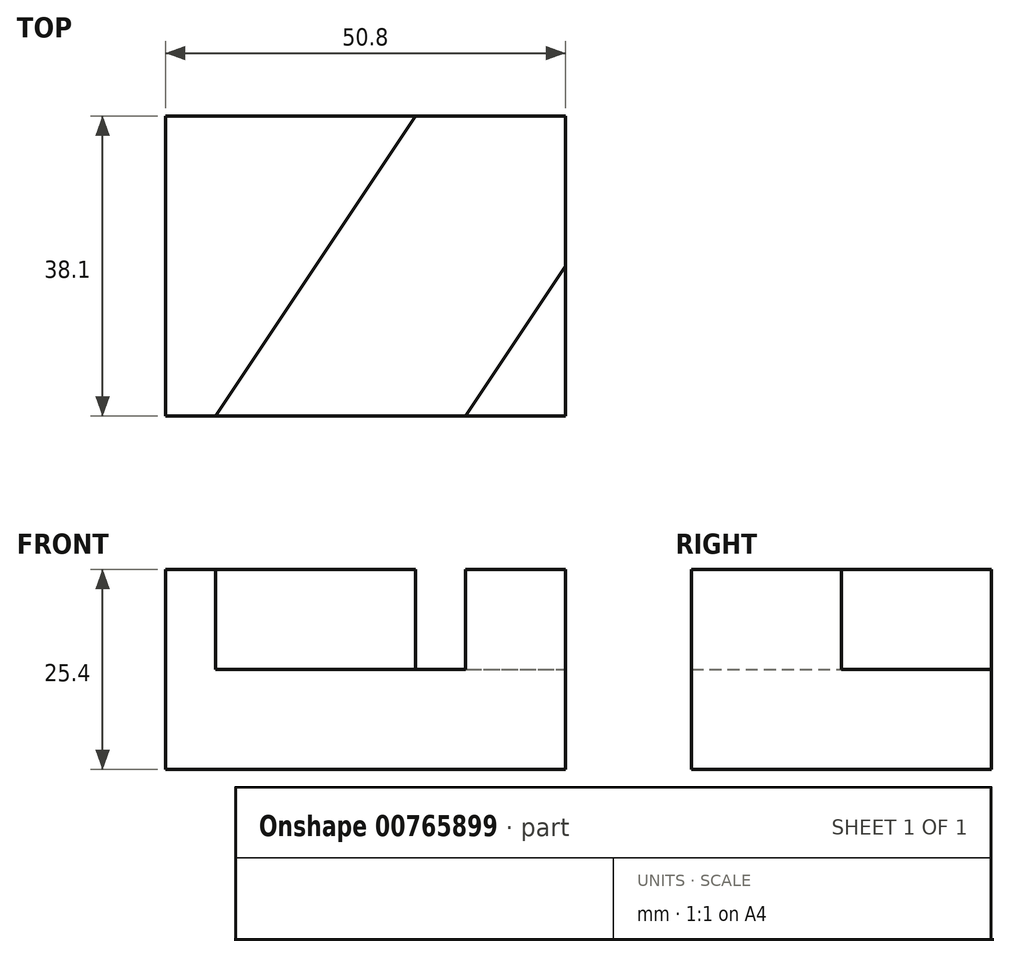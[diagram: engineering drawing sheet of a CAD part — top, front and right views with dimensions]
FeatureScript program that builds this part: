
annotation { "Feature Type Name" : "Feature", "Feature Type Description" : "" }
export const myFeature = defineFeature(function(context is Context, id is Id, definition is map)
    precondition{}
    {
        {
            var Q0;
            Q0=qCreatedBy(makeId("Top.planeOp"),FACE);
            var sketch = newSketch(context, id + "F0", { "sketchPlane" : qUnion([Q0])});
            skLineSegment(sketch, "E0", {"start": v(0, 0) * mm, "end": v(0, 38.1) * mm});
            skLineSegment(sketch, "E1", {"start": v(0, 38.1) * mm, "end": v(50.8, 38.1) * mm});
            skLineSegment(sketch, "E2", {"start": v(50.8, 38.1) * mm, "end": v(50.8, 0) * mm});
            skLineSegment(sketch, "E3", {"start": v(0, 0) * mm, "end": v(50.8, 0) * mm});
            skLineSegment(sketch, "E4", {"start": v(0, 38.1) * mm, "end": v(31.75, 38.1) * mm});
            skLineSegment(sketch, "E5", {"start": v(0, 0) * mm, "end": v(6.35, 0) * mm});
            skLineSegment(sketch, "E6", {"start": v(6.35, 0) * mm, "end": v(31.75, 38.1) * mm});
            skLineSegment(sketch, "E7", {"start": v(50.8, 0) * mm, "end": v(50.8, 19.05) * mm});
            skLineSegment(sketch, "E8", {"start": v(50.8, 0) * mm, "end": v(38.1, 0) * mm});
            skLineSegment(sketch, "E9", {"start": v(38.1, 0) * mm, "end": v(50.8, 19.05) * mm});
            skSolve(sketch);
        }
        {
            var Q0;
            Q0 = qSketchRegion(id + "F0", true);
            extrude(context, id + "F1", {"entities" : qUnion([Q0]), "depth" : 12.7 * mm, "offsetDistance" : 25.4 * mm});
        }
        {
            var Q0;
            Q0=makeQuery(id+"F1.opExtrude","CAP_FACE",FACE,{"disambiguationData":[OSD([sQuery(id+"F0.wireOp",EDGE,"E0"),sQuery(id+"F0.wireOp",EDGE,"E1"),sQuery(id+"F0.wireOp",EDGE,"E2"),sQuery(id+"F0.wireOp",EDGE,"E3"),sQuery(id+"F0.wireOp",EDGE,"E4"),sQuery(id+"F0.wireOp",EDGE,"E5"),sQuery(id+"F0.wireOp",EDGE,"E7"),sQuery(id+"F0.wireOp",EDGE,"E8")])],"isStart":false});
            var sketch = newSketch(context, id + "F2", { "sketchPlane" : qUnion([Q0])});
            skLineSegment(sketch, "E10", {"start": v(0, 0) * mm, "end": v(6.35, 0) * mm});
            skLineSegment(sketch, "E11", {"start": v(0, 38.1) * mm, "end": v(31.75, 38.1) * mm});
            skLineSegment(sketch, "E12", {"start": v(31.75, 38.1) * mm, "end": v(6.35, 0) * mm});
            skLineSegment(sketch, "E13", {"start": v(50.8, 0) * mm, "end": v(50.8, 19.05) * mm});
            skLineSegment(sketch, "E14", {"start": v(50.8, 0) * mm, "end": v(38.1, 0) * mm});
            skLineSegment(sketch, "E15", {"start": v(38.1, 0) * mm, "end": v(50.8, 19.05) * mm});
            skSolve(sketch);
        }
        {
            var Q0;
            Q0 = qSketchRegion(id + "F2", true);
            var Q1;
            Q1=makeQuery(id+"F2.imprint","IMPRINT",FACE,{"disambiguationData":[TD([[makeQuery(id+"F2.imprint","IMPRINT",EDGE,{"derivedFrom":sQuery(id+"F2.wireOp",EDGE,"E10")}),1.0]])]});
            extrude(context, id + "F3", {"entities" : qUnion([Q0, Q1]), "operationType" : NewBodyOperationType.ADD, "depth" : 12.7 * mm, "offsetDistance" : 25.4 * mm});
        }
    });
